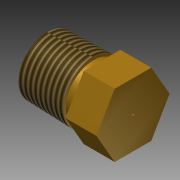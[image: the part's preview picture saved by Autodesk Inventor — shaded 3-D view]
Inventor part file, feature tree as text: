
AUTODESK INVENTOR PART (.ipt)
format: ipt  version: 2011 (Build 150239000, 239)  size: 93,696 bytes
history: native  units: mm (DEFAULTED — no unit token found)
features: thread x2, sketch x1, imported_body x1
ambient origin geometry x8: Origin, YZ Plane, XZ Plane, XY Plane, X Axis, Y Axis, Z Axis, Center Point
bodies: Solid1 (feature_tree)
feature tree (4):
  sketch  "Sketch1"
  imported_body  "Base1"
  thread  "Thread1"  [1 undecoded]
  thread  "Thread2"  [1 undecoded]
note: 2 required parameter values undecoded (feature->parameter linkage not recoverable at this tier; creation-order binding heuristic only, values carry confidence <= 0.55)
